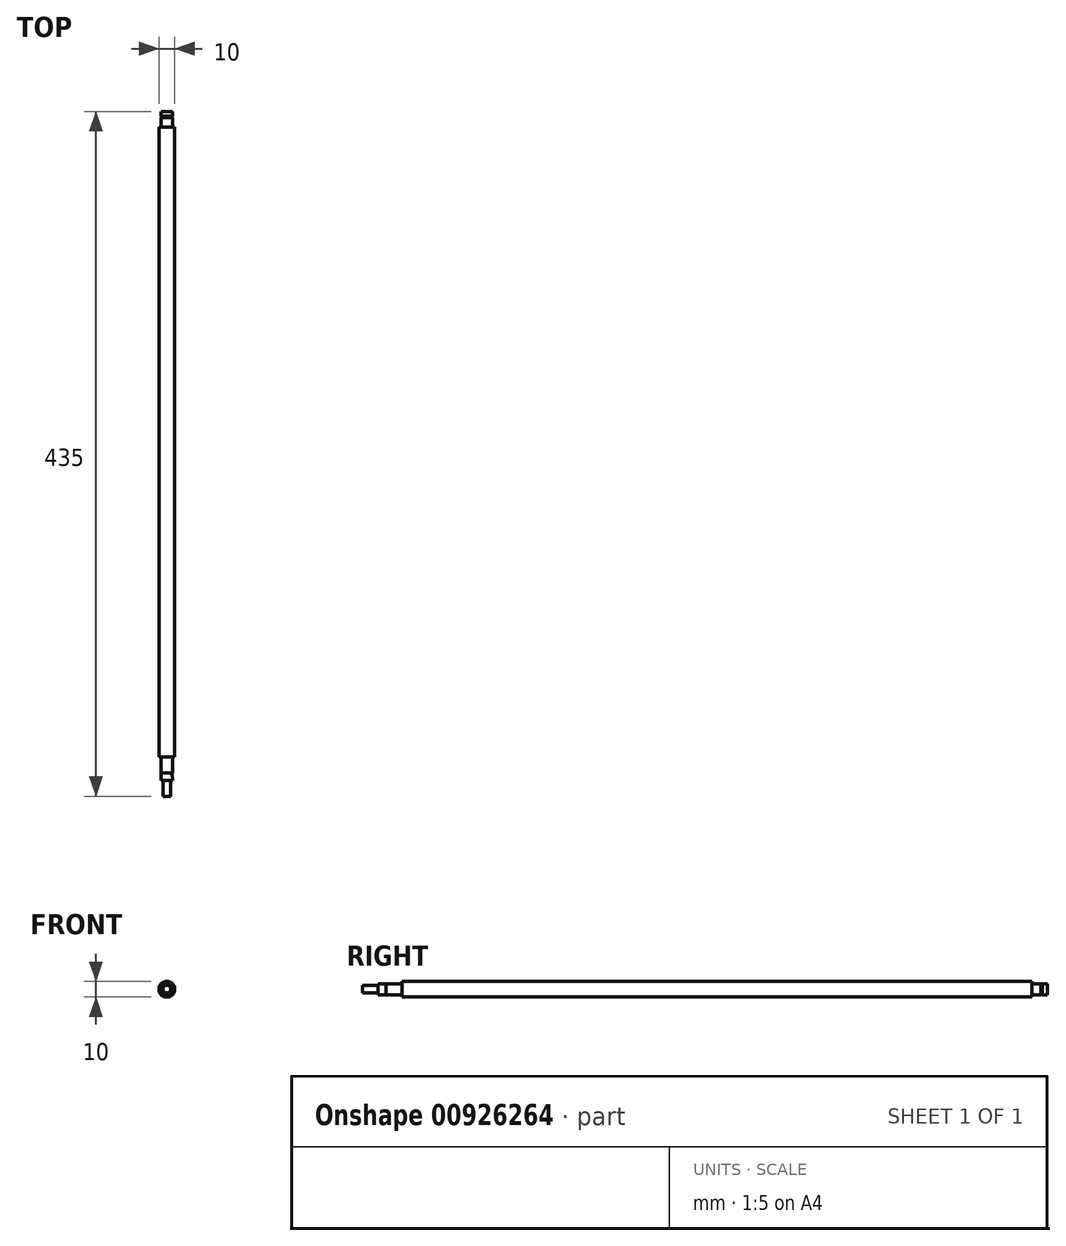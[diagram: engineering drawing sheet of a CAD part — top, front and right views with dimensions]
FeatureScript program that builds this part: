
annotation { "Feature Type Name" : "Feature", "Feature Type Description" : "" }
export const myFeature = defineFeature(function(context is Context, id is Id, definition is map)
    precondition{}
    {
        {
            var Q0;
            Q0=qCreatedBy(makeId("Right.planeOp"),FACE);
            var sketch = newSketch(context, id + "F0", { "sketchPlane" : qUnion([Q0])});
            skLineSegment(sketch, "E0.bottom", {"start": v(200, 5) * mm, "end": v(-200, 5) * mm});
            skLineSegment(sketch, "E0.top", {"start": v(200, -5) * mm, "end": v(-200, -5) * mm});
            skLineSegment(sketch, "E0.left", {"start": v(200, 5) * mm, "end": v(200, -5) * mm});
            skLineSegment(sketch, "E0.right", {"start": v(-200, 5) * mm, "end": v(-200, -5) * mm});
            skPoint(sketch, "E0.middle", {"position": v(0, 0) * mm});
            skLineSegment(sketch, "E1.bottom", {"start": v(-200, 3.5) * mm, "end": v(-210, 3.5) * mm});
            skLineSegment(sketch, "E1.top", {"start": v(-200, -3.5) * mm, "end": v(-210, -3.5) * mm});
            skLineSegment(sketch, "E1.left", {"start": v(-200, 3.5) * mm, "end": v(-200, -3.5) * mm});
            skLineSegment(sketch, "E1.right", {"start": v(-215, 3.5) * mm, "end": v(-215, -3.5) * mm});
            skPoint(sketch, "E1.middle", {"position": v(-207.5, 0) * mm});
            skLineSegment(sketch, "E2.bottom", {"start": v(-215, 2.5) * mm, "end": v(-225, 2.5) * mm});
            skLineSegment(sketch, "E2.top", {"start": v(-215, -2.5) * mm, "end": v(-225, -2.5) * mm});
            skLineSegment(sketch, "E2.left", {"start": v(-215, 2.5) * mm, "end": v(-215, -2.5) * mm});
            skLineSegment(sketch, "E2.right", {"start": v(-225, 2.5) * mm, "end": v(-225, -2.5) * mm});
            skPoint(sketch, "E2.middle", {"position": v(-220, 0) * mm});
            skLineSegment(sketch, "E3.bottom", {"start": v(200, 3.5) * mm, "end": v(206, 3.5) * mm});
            skLineSegment(sketch, "E3.top", {"start": v(200, -3.5) * mm, "end": v(206, -3.5) * mm});
            skLineSegment(sketch, "E3.left", {"start": v(200, 3.5) * mm, "end": v(200, -3.5) * mm});
            skLineSegment(sketch, "E3.right", {"start": v(206, 3.5) * mm, "end": v(206, -3.5) * mm});
            skPoint(sketch, "E3.middle", {"position": v(203, 0) * mm});
            skLineSegment(sketch, "E4", {"start": v(-210, 3.5) * mm, "end": v(-210, -3.5) * mm});
            skLineSegment(sketch, "E5.bottom", {"start": v(206, 3.25) * mm, "end": v(206.9, 3.25) * mm});
            skLineSegment(sketch, "E5.top", {"start": v(206, -3.25) * mm, "end": v(206.9, -3.25) * mm});
            skLineSegment(sketch, "E5.left", {"start": v(206, 3.25) * mm, "end": v(206, -3.25) * mm});
            skLineSegment(sketch, "E5.right", {"start": v(206.9, 3.25) * mm, "end": v(206.9, -3.25) * mm});
            skPoint(sketch, "E5.middle", {"position": v(206.45, 0) * mm});
            skLineSegment(sketch, "E6.bottom", {"start": v(206.9, 3.5) * mm, "end": v(210, 3.5) * mm});
            skLineSegment(sketch, "E6.top", {"start": v(206.9, -3.5) * mm, "end": v(210, -3.5) * mm});
            skLineSegment(sketch, "E6.left", {"start": v(206.9, 3.5) * mm, "end": v(206.9, -3.5) * mm});
            skLineSegment(sketch, "E6.right", {"start": v(210, 3.5) * mm, "end": v(210, -3.5) * mm});
            skPoint(sketch, "E6.middle", {"position": v(208.45, 0) * mm});
            skLineSegment(sketch, "E7", {"start": v(-225, 0) * mm, "end": v(210, 0) * mm});
            skLineSegment(sketch, "E8", {"start": v(-215, 3.5) * mm, "end": v(-210, 3.49) * mm});
            skLineSegment(sketch, "E9", {"start": v(-215, -3.5) * mm, "end": v(-210, -3.49) * mm});
            skSolve(sketch);
        }
        {
            var Q0;
            {var subQ1=sQuery(id+"F0.wireOp",EDGE,"E0.bottom");Q0=makeQuery(id+"F0.imprint","IMPRINT",FACE,{"disambiguationData":[TD([[makeQuery(id+"F0.imprint","IMPRINT",EDGE,{"derivedFrom":subQ1}),1.0]])]});}
            var Q1;
            {var subQ1=sQuery(id+"F0.wireOp",EDGE,"E1.bottom");var subQ3=sQuery(id+"F0.wireOp",EDGE,"E4");var subQ4=makeQuery(id+"F0.imprint","INTERSECT",VERTEX,{"derivedFrom":[subQ1,subQ3]});Q1=makeQuery(id+"F0.imprint","IMPRINT",FACE,{"disambiguationData":[TD([[makeQuery(id+"F0.imprint","IMPRINT",EDGE,{"disambiguationData":[TD([[subQ4,-1.0]])],"derivedFrom":subQ3}),1.0]])]});}
            var Q2;
            {var subQ1=sQuery(id+"F0.wireOp",EDGE,"E1.bottom");var subQ6=sQuery(id+"F0.wireOp",EDGE,"E1.right");var subQ9=makeQuery(id+"F0.imprint","INTERSECT",VERTEX,{"derivedFrom":[subQ1,subQ6]});Q2=makeQuery(id+"F0.imprint","IMPRINT",FACE,{"disambiguationData":[TD([[makeQuery(id+"F0.imprint","IMPRINT",EDGE,{"disambiguationData":[TD([[subQ9,1.0]])],"derivedFrom":subQ1}),1.0]])]});}
            var Q3;
            {var subQ0=sQuery(id+"F0.wireOp",EDGE,"E2.bottom");Q3=makeQuery(id+"F0.imprint","IMPRINT",FACE,{"disambiguationData":[TD([[makeQuery(id+"F0.imprint","IMPRINT",EDGE,{"derivedFrom":subQ0}),1.0]])]});}
            var Q4;
            {var subQ1=sQuery(id+"F0.wireOp",EDGE,"E3.bottom");Q4=makeQuery(id+"F0.imprint","IMPRINT",FACE,{"disambiguationData":[TD([[makeQuery(id+"F0.imprint","IMPRINT",EDGE,{"derivedFrom":subQ1}),-1.0]])]});}
            var Q5;
            {var subQ0=sQuery(id+"F0.wireOp",EDGE,"E5.bottom");Q5=makeQuery(id+"F0.imprint","IMPRINT",FACE,{"disambiguationData":[TD([[makeQuery(id+"F0.imprint","IMPRINT",EDGE,{"derivedFrom":subQ0}),-1.0]])]});}
            var Q6;
            {var subQ1=sQuery(id+"F0.wireOp",EDGE,"E6.bottom");Q6=makeQuery(id+"F0.imprint","IMPRINT",FACE,{"disambiguationData":[TD([[makeQuery(id+"F0.imprint","IMPRINT",EDGE,{"derivedFrom":subQ1}),-1.0]])]});}
            var Q7;
            {var subQ7=sQuery(id+"F0.wireOp",EDGE,"E8");Q7=makeQuery(id+"F0.imprint","IMPRINT",FACE,{"disambiguationData":[TD([[makeQuery(id+"F0.imprint","IMPRINT",EDGE,{"derivedFrom":subQ7}),-1.0]])]});}
            var Q8;
            Q8=sQuery(id+"F0.wireOp",EDGE,"E7");
            revolve(context, id + "F1", {"surfaceOperationType" : NewSurfaceOperationType.NEW, "entities" : qUnion([Q0, Q1, Q2, Q3, Q4, Q5, Q6, Q7]), "axis" : qUnion([Q8]), "revolveType" : RevolveType.FULL});
        }
    });
